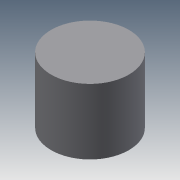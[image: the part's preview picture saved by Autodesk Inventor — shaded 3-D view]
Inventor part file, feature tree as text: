
AUTODESK INVENTOR PART (.ipt)
format: ipt  version: 2013 (Build 170138000, 138)  size: 78,336 bytes
history: native  units: mm
features: sketch x2, extrude x1, plane x1, hole x1
ambient origin geometry x8: Origin, YZ Plane, XZ Plane, XY Plane, X Axis, Y Axis, Z Axis, Center Point
bodies: Solid1 (feature_tree)
feature tree (5):
  extrude  "Extrusion1"  Depth=11.2mm TaperAngle=0.0deg
  plane  "Work Plane1"
  hole  "Hole1"  [1 undecoded]
  sketch  "Sketch1"  dims[d0=13.3mm d1=11.2mm d2=0.0mm]
  sketch  "Sketch3"  dims[d8=2.4mm d9=2.459mm d10=6.65mm d11=4.0mm d12=2.0mm d13=90.0deg d14=6.65mm d15=0.0mm]
note: 1 required parameter value undecoded (feature->parameter linkage not recoverable at this tier; creation-order binding heuristic only, values carry confidence <= 0.55)
